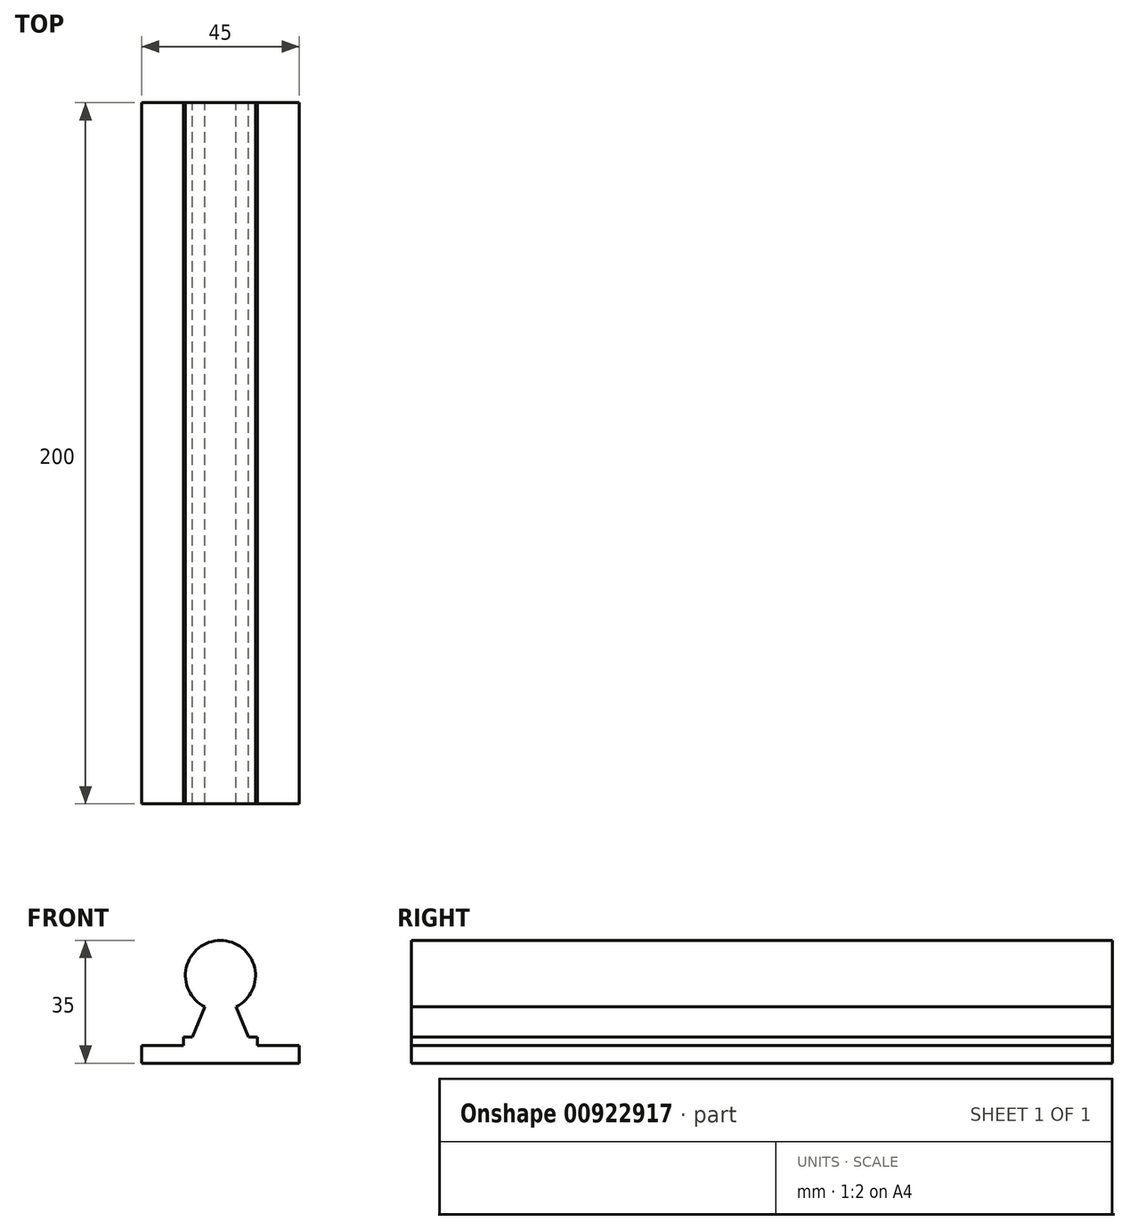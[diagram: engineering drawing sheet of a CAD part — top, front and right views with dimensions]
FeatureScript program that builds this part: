
annotation { "Feature Type Name" : "Feature", "Feature Type Description" : "" }
export const myFeature = defineFeature(function(context is Context, id is Id, definition is map)
    precondition{}
    {
        {
            var Q0;
            Q0=qCreatedBy(makeId("Front.planeOp"),FACE);
            var sketch = newSketch(context, id + "F0", { "sketchPlane" : qUnion([Q0])});
            skCircle(sketch, "E0", {"center": v(0, 0) * mm, "radius": 10 * mm});
            skLineSegment(sketch, "E1", {"start": v(-22.5, -25) * mm, "end": v(22.5, -25) * mm});
            skPoint(sketch, "E2", {"position": v(0, -25) * mm});
            skLineSegment(sketch, "E3", {"start": v(-22.5, -25) * mm, "end": v(-22.5, -20) * mm});
            skLineSegment(sketch, "E4", {"start": v(-22.5, -20) * mm, "end": v(-10.5, -20) * mm});
            skLineSegment(sketch, "E5", {"start": v(-10.5, -20) * mm, "end": v(-10.5, -17.5) * mm});
            skLineSegment(sketch, "E6", {"start": v(-10.5, -17.5) * mm, "end": v(-8, -17.5) * mm});
            skLineSegment(sketch, "E7", {"start": v(-8, -17.5) * mm, "end": v(-4.5, -8.93) * mm});
            skLineSegment(sketch, "E8", {"start": v(0, -29.05) * mm, "end": v(0, 13.28) * mm, "construction": true});
            skLineSegment(sketch, "E9.MirrorCS", {"start": v(8, -17.5) * mm, "end": v(4.5, -8.93) * mm});
            skLineSegment(sketch, "E10.MirrorCS", {"start": v(10.5, -17.5) * mm, "end": v(8, -17.5) * mm});
            skLineSegment(sketch, "E11.MirrorCS", {"start": v(10.5, -20) * mm, "end": v(10.5, -17.5) * mm});
            skLineSegment(sketch, "E12.MirrorCS", {"start": v(22.5, -20) * mm, "end": v(10.5, -20) * mm});
            skLineSegment(sketch, "E13.MirrorCS", {"start": v(22.5, -25) * mm, "end": v(22.5, -20) * mm});
            skSolve(sketch);
        }
        {
            var Q0;
            Q0 = qSketchRegion(id + "F0", true);
            extrude(context, id + "F1", {"entities" : qUnion([Q0]), "depth" : 200 * mm, "offsetDistance" : 25 * mm});
        }
    });
